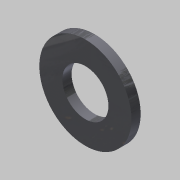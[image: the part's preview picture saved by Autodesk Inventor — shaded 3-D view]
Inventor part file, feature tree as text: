
AUTODESK INVENTOR PART (.ipt)
format: ipt  version: 2012 SP1 (Build 160190100, 190)  size: 78,336 bytes
history: native  units: in
note: dims shown in document units (in); Inventor stores cm internally (conversion verified against a paired STEP export)
features: extrude x1, sketch x1
ambient origin geometry x8: Origin, YZ Plane, XZ Plane, XY Plane, X Axis, Y Axis, Z Axis, Center Point
bodies: Solid1 (feature_tree)
feature tree (2):
  extrude  "Extrusion1"  Depth=0.3937in
  sketch  "Sketch1"  dims[d0=0.1969in d1=0.3937in d2=0.0394in d3=0.0in]
